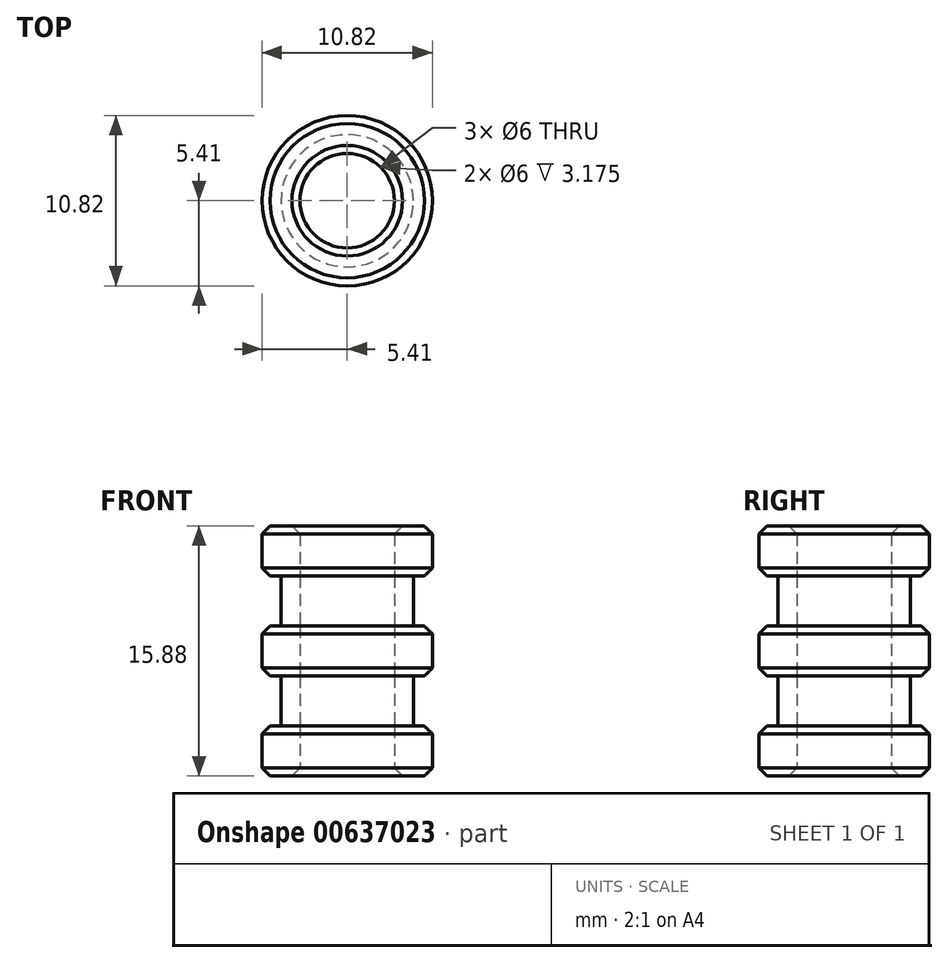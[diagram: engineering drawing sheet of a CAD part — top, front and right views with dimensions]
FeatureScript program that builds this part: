
annotation { "Feature Type Name" : "Feature", "Feature Type Description" : "" }
export const myFeature = defineFeature(function(context is Context, id is Id, definition is map)
    precondition{}
    {
        {
            var Q0;
            Q0=qCreatedBy(makeId("Top.planeOp"),FACE);
            var sketch = newSketch(context, id + "F0", { "sketchPlane" : qUnion([Q0])});
            skCircle(sketch, "E0", {"center": v(0, 0) * mm, "radius": 3 * mm});
            skCircle(sketch, "E1", {"center": v(0, 0) * mm, "radius": 4.2 * mm});
            skCircle(sketch, "E2", {"center": v(0, 0) * mm, "radius": 5.4 * mm});
            skSolve(sketch);
        }
        {
            var Q0;
            Q0=makeQuery(id+"F0.imprint","IMPRINT",FACE,{"disambiguationData":[TD([[makeQuery(id+"F0.imprint","IMPRINT",EDGE,{"derivedFrom":sQuery(id+"F0.wireOp",EDGE,"E1")}),-1.0]])]});
            var Q1;
            Q1=makeQuery(id+"F0.imprint","IMPRINT",FACE,{"disambiguationData":[TD([[makeQuery(id+"F0.imprint","IMPRINT",EDGE,{"derivedFrom":sQuery(id+"F0.wireOp",EDGE,"E0")}),-1.0]])]});
            extrude(context, id + "F1", {"entities" : qUnion([Q0, Q1]), "depth" : 3.17 * mm, "offsetDistance" : 25.4 * mm});
        }
        {
            var Q0;
            Q0=makeQuery(id+"F1.opExtrude","SWEPT_BODY",BODY,{"disambiguationData":[OSD([sQuery(id+"F0.wireOp",EDGE,"E0"),sQuery(id+"F0.wireOp",EDGE,"E2")])]});
            transform(context, id + "F2", {"entities" : qUnion([Q0]), "transformType" : TransformType.TRANSLATION_3D, "dx" : 0 * mm, "dy" : 0 * mm, "dz" : 15.88 * mm, "makeCopy" : false});
        }
        {
            var Q0;
            Q0=makeQuery(id+"F0.imprint","IMPRINT",FACE,{"disambiguationData":[TD([[makeQuery(id+"F0.imprint","IMPRINT",EDGE,{"derivedFrom":sQuery(id+"F0.wireOp",EDGE,"E0")}),-1.0]])]});
            extrude(context, id + "F3", {"entities" : qUnion([Q0]), "depth" : 3.17 * mm, "offsetDistance" : 25.4 * mm});
        }
        {
            var Q0;
            Q0=makeQuery(id+"F3.opExtrude","SWEPT_BODY",BODY,{"disambiguationData":[OSD([sQuery(id+"F0.wireOp",EDGE,"E0"),sQuery(id+"F0.wireOp",EDGE,"E1")])]});
            transform(context, id + "F4", {"entities" : qUnion([Q0]), "transformType" : TransformType.TRANSLATION_3D, "dx" : 0 * mm, "dy" : 0 * mm, "dz" : 12.7 * mm, "makeCopy" : false});
        }
        {
            var Q0;
            Q0=makeQuery(id+"F0.imprint","IMPRINT",FACE,{"disambiguationData":[TD([[makeQuery(id+"F0.imprint","IMPRINT",EDGE,{"derivedFrom":sQuery(id+"F0.wireOp",EDGE,"E1")}),-1.0]])]});
            var Q1;
            Q1=makeQuery(id+"F0.imprint","IMPRINT",FACE,{"disambiguationData":[TD([[makeQuery(id+"F0.imprint","IMPRINT",EDGE,{"derivedFrom":sQuery(id+"F0.wireOp",EDGE,"E0")}),-1.0]])]});
            extrude(context, id + "F5", {"entities" : qUnion([Q0, Q1]), "depth" : 3.17 * mm, "offsetDistance" : 25.4 * mm});
        }
        {
            var Q0;
            Q0=makeQuery(id+"F5.opExtrude","SWEPT_BODY",BODY,{"disambiguationData":[OSD([sQuery(id+"F0.wireOp",EDGE,"E0"),sQuery(id+"F0.wireOp",EDGE,"E2")])]});
            transform(context, id + "F6", {"entities" : qUnion([Q0]), "transformType" : TransformType.TRANSLATION_3D, "dx" : 0 * mm, "dy" : 0 * mm, "dz" : 9.52 * mm, "makeCopy" : false});
        }
        {
            var Q0;
            Q0=makeQuery(id+"F0.imprint","IMPRINT",FACE,{"disambiguationData":[TD([[makeQuery(id+"F0.imprint","IMPRINT",EDGE,{"derivedFrom":sQuery(id+"F0.wireOp",EDGE,"E0")}),-1.0]])]});
            extrude(context, id + "F7", {"entities" : qUnion([Q0]), "depth" : 3.17 * mm, "offsetDistance" : 25.4 * mm});
        }
        {
            var Q0;
            Q0=makeQuery(id+"F7.opExtrude","SWEPT_BODY",BODY,{"disambiguationData":[OSD([sQuery(id+"F0.wireOp",EDGE,"E0"),sQuery(id+"F0.wireOp",EDGE,"E1")])]});
            transform(context, id + "F8", {"entities" : qUnion([Q0]), "transformType" : TransformType.TRANSLATION_3D, "dx" : 0 * mm, "dy" : 0 * mm, "dz" : 6.35 * mm, "makeCopy" : false});
        }
        {
            var Q0;
            Q0=makeQuery(id+"F0.imprint","IMPRINT",FACE,{"disambiguationData":[TD([[makeQuery(id+"F0.imprint","IMPRINT",EDGE,{"derivedFrom":sQuery(id+"F0.wireOp",EDGE,"E1")}),-1.0]])]});
            var Q1;
            Q1=makeQuery(id+"F0.imprint","IMPRINT",FACE,{"disambiguationData":[TD([[makeQuery(id+"F0.imprint","IMPRINT",EDGE,{"derivedFrom":sQuery(id+"F0.wireOp",EDGE,"E0")}),-1.0]])]});
            extrude(context, id + "F9", {"entities" : qUnion([Q0, Q1]), "depth" : 3.17 * mm, "offsetDistance" : 25.4 * mm});
        }
        {
            var Q0;
            Q0=makeQuery(id+"F7.opExtrude","SWEPT_BODY",BODY,{"disambiguationData":[OSD([sQuery(id+"F0.wireOp",EDGE,"E0"),sQuery(id+"F0.wireOp",EDGE,"E1")])]});
            transform(context, id + "F10", {"entities" : qUnion([Q0]), "transformType" : TransformType.TRANSLATION_3D, "dx" : 0 * mm, "dy" : 0 * mm, "dz" : -3.17 * mm, "makeCopy" : false});
        }
        {
            var Q0;
            Q0=makeQuery(id+"F5.opExtrude","SWEPT_BODY",BODY,{"disambiguationData":[OSD([sQuery(id+"F0.wireOp",EDGE,"E0"),sQuery(id+"F0.wireOp",EDGE,"E2")])]});
            transform(context, id + "F11", {"entities" : qUnion([Q0]), "transformType" : TransformType.TRANSLATION_3D, "dx" : 0 * mm, "dy" : 0 * mm, "dz" : -3.17 * mm, "makeCopy" : false});
        }
        {
            var Q0;
            Q0=makeQuery(id+"F3.opExtrude","SWEPT_BODY",BODY,{"disambiguationData":[OSD([sQuery(id+"F0.wireOp",EDGE,"E0"),sQuery(id+"F0.wireOp",EDGE,"E1")])]});
            transform(context, id + "F12", {"entities" : qUnion([Q0]), "transformType" : TransformType.TRANSLATION_3D, "dx" : 0 * mm, "dy" : 0 * mm, "dz" : -3.17 * mm, "makeCopy" : false});
        }
        {
            var Q0;
            Q0=makeQuery(id+"F1.opExtrude","SWEPT_BODY",BODY,{"disambiguationData":[OSD([sQuery(id+"F0.wireOp",EDGE,"E0"),sQuery(id+"F0.wireOp",EDGE,"E2")])]});
            transform(context, id + "F13", {"entities" : qUnion([Q0]), "transformType" : TransformType.TRANSLATION_3D, "dx" : 0 * mm, "dy" : 0 * mm, "dz" : -3.17 * mm, "makeCopy" : false});
        }
        {
            var Q0;
            Q0=makeQuery(id+"F1.opExtrude","CAP_EDGE",EDGE,{"disambiguationData":[OSD([sQuery(id+"F0.wireOp",EDGE,"E0")])],"isStart":false});
            var Q1;
            Q1=makeQuery(id+"F1.opExtrude","CAP_EDGE",EDGE,{"disambiguationData":[OSD([sQuery(id+"F0.wireOp",EDGE,"E2")])],"isStart":false});
            var Q2;
            Q2=makeQuery(id+"F5.opExtrude","CAP_EDGE",EDGE,{"disambiguationData":[OSD([sQuery(id+"F0.wireOp",EDGE,"E2")])],"isStart":false});
            var Q3;
            Q3=makeQuery(id+"F5.opExtrude","CAP_EDGE",EDGE,{"disambiguationData":[OSD([sQuery(id+"F0.wireOp",EDGE,"E2")])],"isStart":true});
            var Q4;
            Q4=makeQuery(id+"F9.opExtrude","CAP_EDGE",EDGE,{"disambiguationData":[OSD([sQuery(id+"F0.wireOp",EDGE,"E2")])],"isStart":false});
            var Q5;
            Q5=makeQuery(id+"F9.opExtrude","CAP_EDGE",EDGE,{"disambiguationData":[OSD([sQuery(id+"F0.wireOp",EDGE,"E2")])],"isStart":true});
            chamfer(context, id + "F14", {"entities" : qUnion([Q0, Q1, Q2, Q3, Q4, Q5]), "width" : 0.5 * mm, "tangentPropagation" : true});
        }
        {
            var Q0;
            Q0=makeQuery(id+"F9.opExtrude","CAP_EDGE",EDGE,{"disambiguationData":[OSD([sQuery(id+"F0.wireOp",EDGE,"E0")])],"isStart":true});
            var Q1;
            Q1=makeQuery(id+"F1.opExtrude","CAP_EDGE",EDGE,{"disambiguationData":[OSD([sQuery(id+"F0.wireOp",EDGE,"E2")])],"isStart":true});
            chamfer(context, id + "F15", {"entities" : qUnion([Q0, Q1]), "width" : 0.5 * mm, "tangentPropagation" : true});
        }
    });
